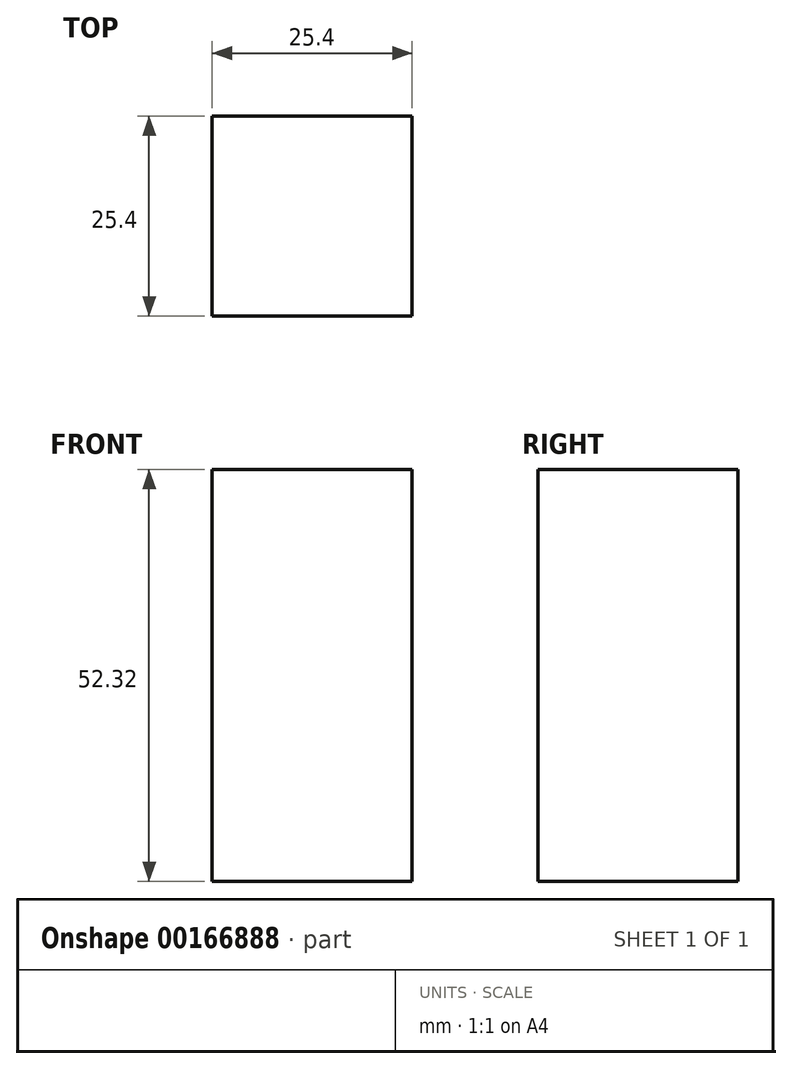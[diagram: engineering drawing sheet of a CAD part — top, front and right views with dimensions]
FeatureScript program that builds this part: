
annotation { "Feature Type Name" : "Feature", "Feature Type Description" : "" }
export const myFeature = defineFeature(function(context is Context, id is Id, definition is map)
    precondition{}
    {
        {
            var Q0;
            Q0=qCreatedBy(makeId("Top.planeOp"),FACE);
            var sketch = newSketch(context, id + "F0", { "sketchPlane" : qUnion([Q0])});
            skLineSegment(sketch, "E0.bottom", {"start": v(0, 0) * mm, "end": v(-25.4, 0) * mm});
            skLineSegment(sketch, "E0.top", {"start": v(0, 25.4) * mm, "end": v(-25.4, 25.4) * mm});
            skLineSegment(sketch, "E0.left", {"start": v(0, 0) * mm, "end": v(0, 25.4) * mm});
            skLineSegment(sketch, "E0.right", {"start": v(-25.4, 0) * mm, "end": v(-25.4, 25.4) * mm});
            skSolve(sketch);
        }
        {
            var Q0;
            Q0 = qSketchRegion(id + "F0", true);
            var Q1;
            Q1=makeQuery(id+"F0.imprint","IMPRINT",FACE,{"disambiguationData":[TD([[makeQuery(id+"F0.imprint","IMPRINT",EDGE,{"derivedFrom":sQuery(id+"F0.wireOp",EDGE,"E0.bottom")}),-1.0]])]});
            extrude(context, id + "F1", {"entities" : qUnion([Q0, Q1]), "depth" : 52.32 * mm});
        }
    });
